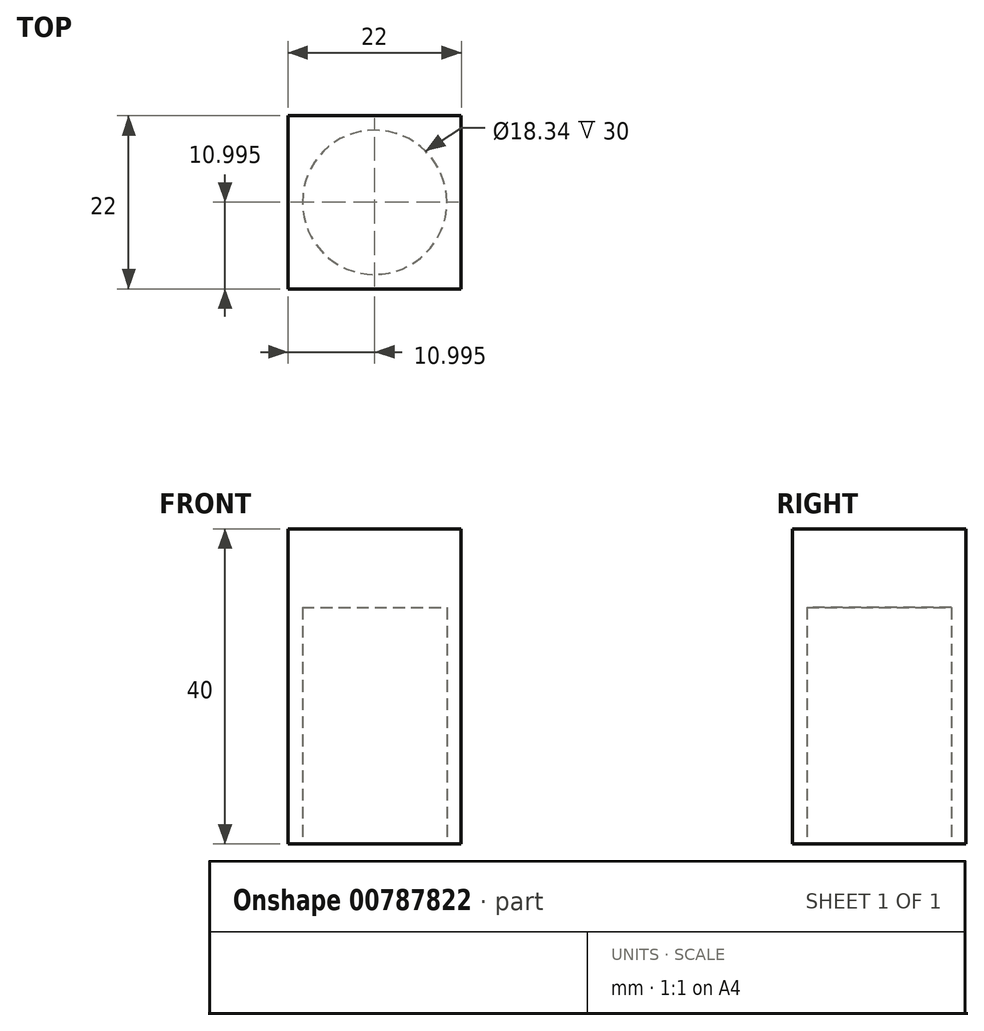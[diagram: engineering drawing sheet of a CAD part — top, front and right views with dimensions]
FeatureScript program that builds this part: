
annotation { "Feature Type Name" : "Feature", "Feature Type Description" : "" }
export const myFeature = defineFeature(function(context is Context, id is Id, definition is map)
    precondition{}
    {
        {
            var Q0;
            Q0=qCreatedBy(makeId("Top.planeOp"),FACE);
            var sketch = newSketch(context, id + "F0", { "sketchPlane" : qUnion([Q0])});
            skLineSegment(sketch, "E0.bottom", {"start": v(-25.5, 14.78) * mm, "end": v(-3.5, 14.78) * mm});
            skLineSegment(sketch, "E0.top", {"start": v(-25.5, -7.22) * mm, "end": v(-3.5, -7.22) * mm});
            skLineSegment(sketch, "E0.left", {"start": v(-25.5, 14.78) * mm, "end": v(-25.5, -7.22) * mm});
            skLineSegment(sketch, "E0.right", {"start": v(-3.5, 14.78) * mm, "end": v(-3.5, -7.22) * mm});
            skSolve(sketch);
        }
        {
            var Q0;
            Q0=makeQuery(id+"F0.imprint","IMPRINT",FACE,{"disambiguationData":[TD([[makeQuery(id+"F0.imprint","IMPRINT",EDGE,{"derivedFrom":sQuery(id+"F0.wireOp",EDGE,"E0.bottom")}),-1.0]])]});
            extrude(context, id + "F1", {"entities" : qUnion([Q0]), "oppositeDirection" : true, "depth" : 40 * mm, "offsetDistance" : 25 * mm});
        }
        {
            var Q0;
            Q0=makeQuery(id+"F1.opExtrude","CAP_FACE",FACE,{"disambiguationData":[OSD([sQuery(id+"F0.wireOp",EDGE,"E0.bottom"),sQuery(id+"F0.wireOp",EDGE,"E0.top"),sQuery(id+"F0.wireOp",EDGE,"E0.left"),sQuery(id+"F0.wireOp",EDGE,"E0.right")])],"isStart":false});
            var sketch = newSketch(context, id + "F2", { "sketchPlane" : qUnion([Q0])});
            skCircle(sketch, "E1", {"center": v(-14.5, -3.78) * mm, "radius": 9.17 * mm});
            skPoint(sketch, "E1.centerSnap0", {"position": v(-25.5, -3.78) * mm});
            skPoint(sketch, "E1.centerSnap1", {"position": v(-14.5, -14.78) * mm});
            skSolve(sketch);
        }
        {
            var Q0;
            Q0=makeQuery(id+"F2.imprint","IMPRINT",FACE,{"disambiguationData":[TD([[makeQuery(id+"F2.imprint","IMPRINT",EDGE,{"derivedFrom":sQuery(id+"F2.wireOp",EDGE,"E1")}),1.0]])]});
            extrude(context, id + "F3", {"entities" : qUnion([Q0]), "operationType" : NewBodyOperationType.REMOVE, "oppositeDirection" : true, "depth" : 30 * mm, "offsetDistance" : 25 * mm});
        }
    });
